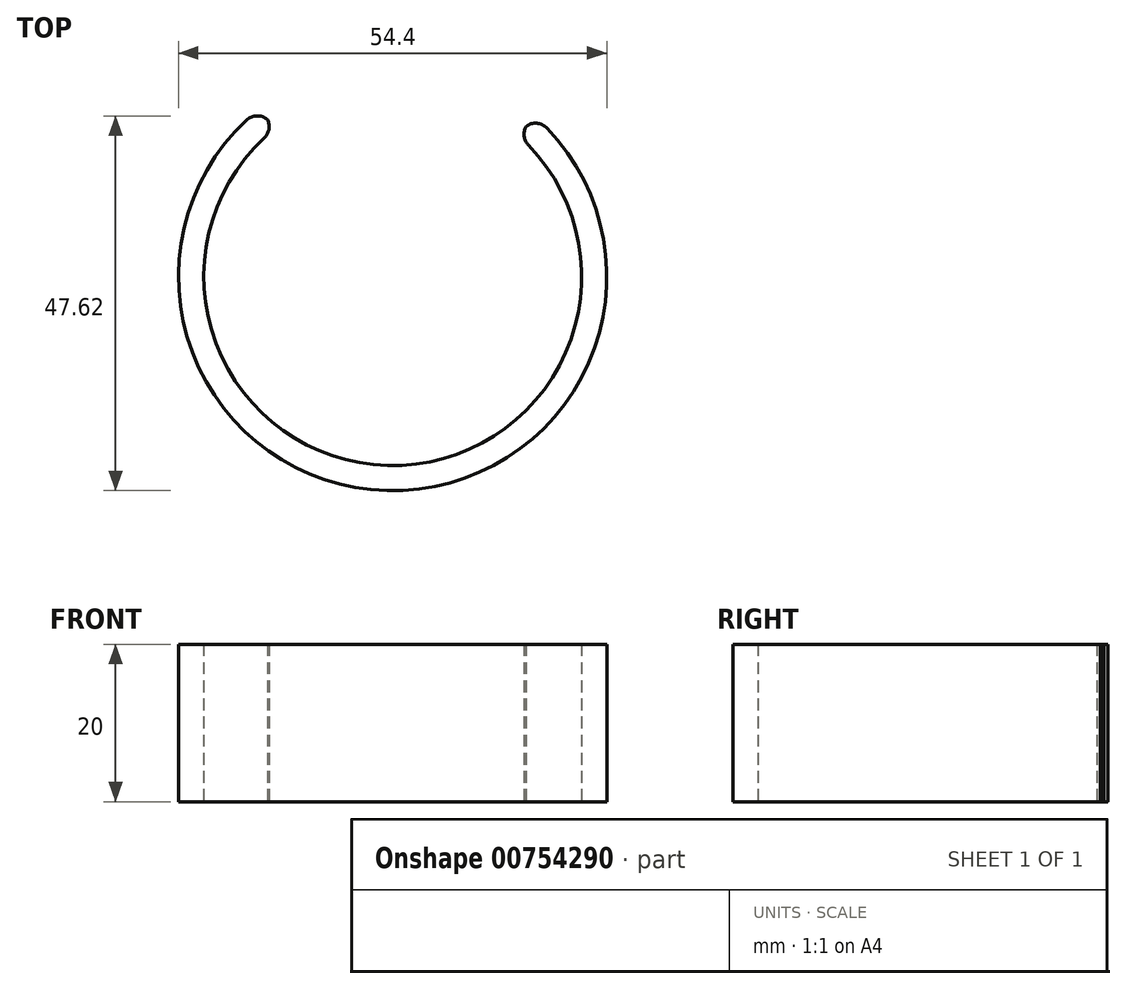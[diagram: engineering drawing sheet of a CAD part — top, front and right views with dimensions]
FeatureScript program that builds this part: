
annotation { "Feature Type Name" : "Feature", "Feature Type Description" : "" }
export const myFeature = defineFeature(function(context is Context, id is Id, definition is map)
    precondition{}
    {
        {
            var Q0;
            Q0=qCreatedBy(makeId("Top.planeOp"),FACE);
            var sketch = newSketch(context, id + "F0", { "sketchPlane" : qUnion([Q0])});
            skCircle(sketch, "E0", {"center": v(0, 0) * mm, "radius": 24 * mm});
            skLineSegment(sketch, "E1", {"start": v(0, 0) * mm, "end": v(0, 43.44) * mm, "construction": true});
            skPoint(sketch, "E1.endSnap0", {"position": v(0, 24.25) * mm});
            skCircle(sketch, "E2", {"center": v(0, 0) * mm, "radius": 27.2 * mm});
            skPoint(sketch, "E3.start.orphan", {"position": v(-27.2, 0) * mm});
            skLineSegment(sketch, "E4", {"start": v(0, 0) * mm, "end": v(25.26, 28.54) * mm});
            skLineSegment(sketch, "E5", {"start": v(0, 0) * mm, "end": v(-25.19, 31.69) * mm});
            skSolve(sketch);
        }
        {
            var Q0;
            {var subQ0=sQuery(id+"F0.wireOp",EDGE,"E4");var subQ1=sQuery(id+"F0.wireOp",EDGE,"E0");var subQ2=makeQuery(id+"F0.imprint","INTERSECT",VERTEX,{"derivedFrom":[subQ1,subQ0]});Q0=makeQuery(id+"F0.imprint","IMPRINT",FACE,{"disambiguationData":[TD([[makeQuery(id+"F0.imprint","IMPRINT",EDGE,{"disambiguationData":[TD([[subQ2,1.0]])],"derivedFrom":subQ1}),-1.0]])]});}
            extrude(context, id + "F1", {"entities" : qUnion([Q0]), "depth" : 20 * mm, "offsetDistance" : 25 * mm});
        }
        {
            var Q0;
            Q0=makeQuery(id+"F1.opExtrude","SWEPT_EDGE",EDGE,{"disambiguationData":[OSD([sQuery(id+"F0.wireOp",EDGE,"E0"),sQuery(id+"F0.wireOp",EDGE,"E5")])]});
            var Q1;
            Q1=makeQuery(id+"F1.opExtrude","SWEPT_EDGE",EDGE,{"disambiguationData":[OSD([sQuery(id+"F0.wireOp",EDGE,"E0"),sQuery(id+"F0.wireOp",EDGE,"E4")])]});
            var Q2;
            Q2=makeQuery(id+"F1.opExtrude","SWEPT_EDGE",EDGE,{"disambiguationData":[OSD([sQuery(id+"F0.wireOp",EDGE,"E2"),sQuery(id+"F0.wireOp",EDGE,"E5")])]});
            var Q3;
            Q3=makeQuery(id+"F1.opExtrude","SWEPT_EDGE",EDGE,{"disambiguationData":[OSD([sQuery(id+"F0.wireOp",EDGE,"E2"),sQuery(id+"F0.wireOp",EDGE,"E4")])]});
            fillet(context, id + "F2", {"entities" : qUnion([Q0, Q1, Q2, Q3]), "radius" : 2 * mm, "tangentPropagation" : true, "allowEdgeOverflow" : false});
        }
    });
